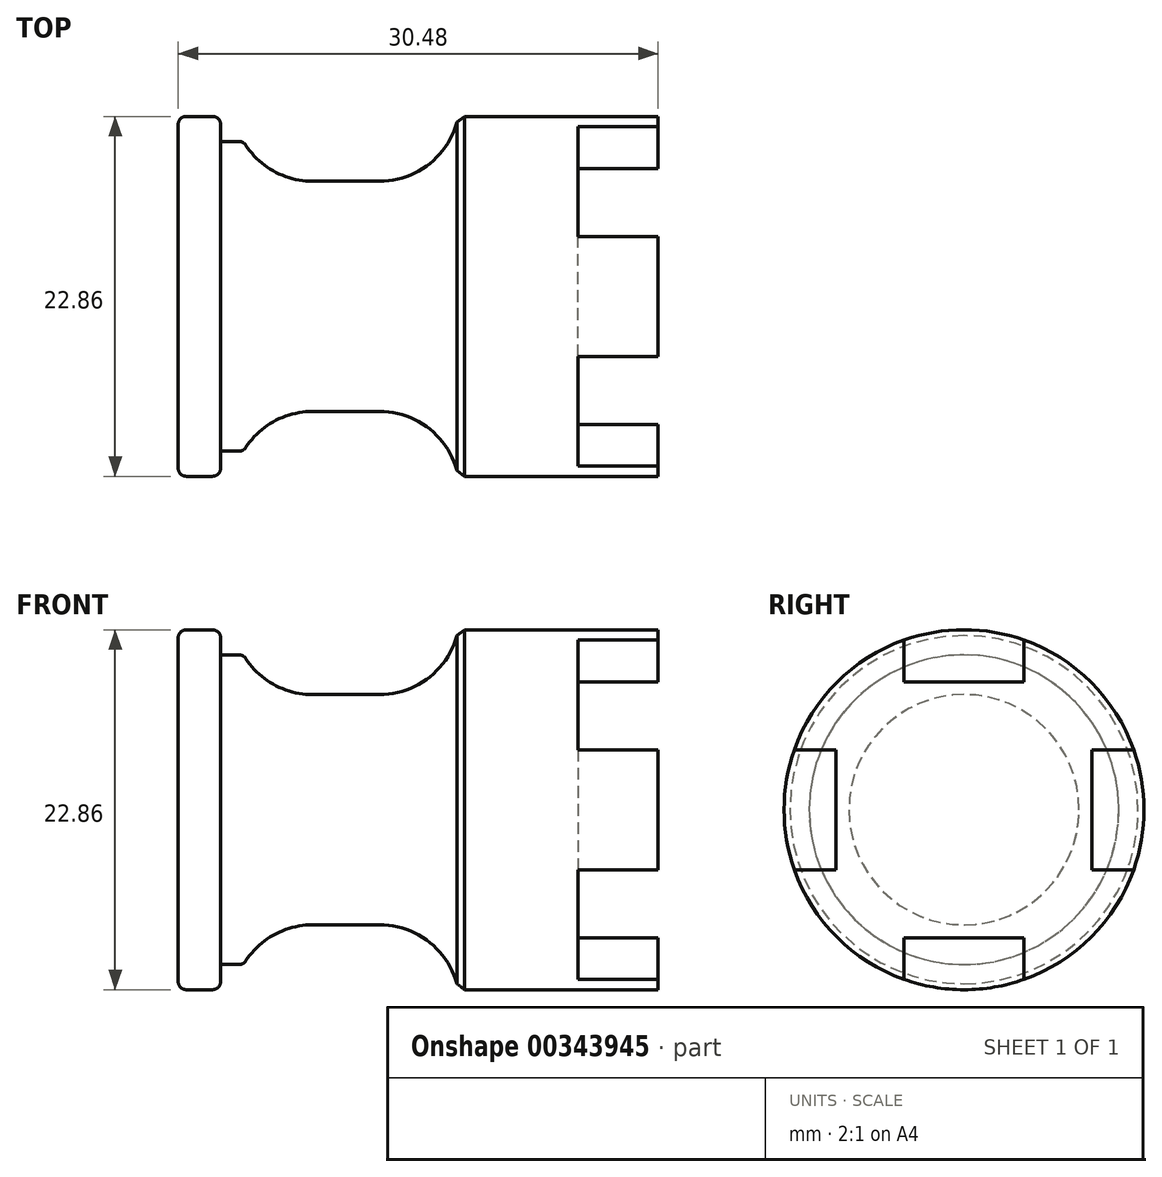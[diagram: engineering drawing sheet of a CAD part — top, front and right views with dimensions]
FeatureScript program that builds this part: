
annotation { "Feature Type Name" : "Feature", "Feature Type Description" : "" }
export const myFeature = defineFeature(function(context is Context, id is Id, definition is map)
    precondition{}
    {
        {
            var Q0;
            Q0=qCreatedBy(makeId("Front.planeOp"),FACE);
            var sketch = newSketch(context, id + "F0", { "sketchPlane" : qUnion([Q0])});
            skLineSegment(sketch, "E0", {"start": v(0, 0) * mm, "end": v(-25.4, 0) * mm});
            skLineSegment(sketch, "E1", {"start": v(-25.4, 0) * mm, "end": v(-25.4, 11.43) * mm});
            skLineSegment(sketch, "E2", {"start": v(-25.4, 11.43) * mm, "end": v(-22.71, 11.43) * mm});
            skLineSegment(sketch, "E3", {"start": v(-22.71, 11.43) * mm, "end": v(-22.71, 9.84) * mm});
            skLineSegment(sketch, "E4", {"start": v(-22.71, 9.84) * mm, "end": v(-21.25, 9.84) * mm});
            skLineSegment(sketch, "E5", {"start": v(-21.25, 9.84) * mm, "end": v(-20.32, 7.31) * mm});
            skLineSegment(sketch, "E6", {"start": v(-20.32, 7.31) * mm, "end": v(-7.62, 7.31) * mm});
            skLineSegment(sketch, "E7", {"start": v(-7.62, 7.31) * mm, "end": v(-7.62, 11.43) * mm});
            skLineSegment(sketch, "E8", {"start": v(-7.62, 11.43) * mm, "end": v(0, 11.43) * mm});
            skLineSegment(sketch, "E9", {"start": v(0, 11.43) * mm, "end": v(0, 0) * mm});
            skSolve(sketch);
        }
        {
            var Q0;
            Q0=makeQuery(id+"F0.imprint","IMPRINT",FACE,{"disambiguationData":[TD([[makeQuery(id+"F0.imprint","IMPRINT",EDGE,{"derivedFrom":sQuery(id+"F0.wireOp",EDGE,"E0")}),-1.0]])]});
            var Q1;
            Q1=sQuery(id+"F0.wireOp",EDGE,"E0");
            revolve(context, id + "F1", {"entities" : qUnion([Q0]), "axis" : qUnion([Q1]), "revolveType" : RevolveType.FULL});
        }
        {
            var Q0;
            Q0=makeQuery(id+"F1.opRevolve","SWEPT_FACE",FACE,{"disambiguationData":[OSD([sQuery(id+"F0.wireOp",EDGE,"E9")])]});
            var sketch = newSketch(context, id + "F2", { "sketchPlane" : qUnion([Q0])});
            skLineSegment(sketch, "E10", {"start": v(-3.81, 10.78) * mm, "end": v(-3.81, 8.13) * mm});
            skLineSegment(sketch, "E11", {"start": v(-3.81, 8.13) * mm, "end": v(3.81, 8.13) * mm});
            skLineSegment(sketch, "E12", {"start": v(3.81, 8.13) * mm, "end": v(3.81, 10.78) * mm});
            skLineSegment(sketch, "E13", {"start": v(10.78, 3.81) * mm, "end": v(8.13, 3.81) * mm});
            skLineSegment(sketch, "E14", {"start": v(8.13, 3.8) * mm, "end": v(8.13, -3.81) * mm});
            skLineSegment(sketch, "E15", {"start": v(8.13, -3.81) * mm, "end": v(10.78, -3.81) * mm});
            skLineSegment(sketch, "E16", {"start": v(-3.81, -10.78) * mm, "end": v(-3.81, -8.13) * mm});
            skLineSegment(sketch, "E17", {"start": v(-3.81, -8.13) * mm, "end": v(3.81, -8.13) * mm});
            skLineSegment(sketch, "E18", {"start": v(3.81, -8.13) * mm, "end": v(3.81, -10.78) * mm});
            skLineSegment(sketch, "E19", {"start": v(-10.78, 3.8) * mm, "end": v(-8.13, 3.8) * mm});
            skLineSegment(sketch, "E20", {"start": v(-8.13, 3.8) * mm, "end": v(-8.13, -3.81) * mm});
            skLineSegment(sketch, "E21", {"start": v(-8.13, -3.81) * mm, "end": v(-10.78, -3.81) * mm});
            skSolve(sketch);
        }
        {
            var Q0;
            {var subQ0=sQuery(id+"F2.wireOp",EDGE,"E10");Q0=makeQuery(id+"F2.imprint","IMPRINT",FACE,{"disambiguationData":[TD([[makeQuery(id+"F2.imprint","IMPRINT",EDGE,{"derivedFrom":subQ0}),1.0]])]});}
            var Q1;
            {var subQ0=sQuery(id+"F2.wireOp",EDGE,"E13");Q1=makeQuery(id+"F2.imprint","IMPRINT",FACE,{"disambiguationData":[TD([[makeQuery(id+"F2.imprint","IMPRINT",EDGE,{"derivedFrom":subQ0}),1.0]])]});}
            var Q2;
            {var subQ0=sQuery(id+"F2.wireOp",EDGE,"E16");Q2=makeQuery(id+"F2.imprint","IMPRINT",FACE,{"disambiguationData":[TD([[makeQuery(id+"F2.imprint","IMPRINT",EDGE,{"derivedFrom":subQ0}),-1.0]])]});}
            var Q3;
            {var subQ0=sQuery(id+"F2.wireOp",EDGE,"E19");Q3=makeQuery(id+"F2.imprint","IMPRINT",FACE,{"disambiguationData":[TD([[makeQuery(id+"F2.imprint","IMPRINT",EDGE,{"derivedFrom":subQ0}),-1.0]])]});}
            extrude(context, id + "F3", {"entities" : qUnion([Q0, Q1, Q2, Q3]), "operationType" : NewBodyOperationType.ADD, "depth" : 5.08 * mm});
        }
        {
            var Q0;
            Q0=makeQuery(id+"F1.opRevolve","SWEPT_EDGE",EDGE,{"disambiguationData":[OSD([sQuery(id+"F0.wireOp",EDGE,"E5"),sQuery(id+"F0.wireOp",EDGE,"E6")])]});
            fillet(context, id + "F4", {"entities" : qUnion([Q0]), "radius" : 5.08 * mm, "tangentPropagation" : true, "allowEdgeOverflow" : false});
        }
        {
            var Q0;
            Q0=makeQuery(id+"F1.opRevolve","SWEPT_EDGE",EDGE,{"disambiguationData":[OSD([sQuery(id+"F0.wireOp",EDGE,"E6"),sQuery(id+"F0.wireOp",EDGE,"E7")])]});
            fillet(context, id + "F5", {"entities" : qUnion([Q0]), "radius" : 5.08 * mm, "tangentPropagation" : true, "allowEdgeOverflow" : false});
        }
        {
            var Q0;
            Q0=makeQuery(id+"F4.opFillet","BLEND_EDGE",EDGE,{"blendedFrom":[makeQuery(id+"F1.opRevolve","SWEPT_EDGE",EDGE,{"disambiguationData":[OSD([sQuery(id+"F0.wireOp",EDGE,"E5"),sQuery(id+"F0.wireOp",EDGE,"E6")])]}),makeQuery(id+"F1.opRevolve","SWEPT_FACE",FACE,{"disambiguationData":[OSD([sQuery(id+"F0.wireOp",EDGE,"E4")])]})],"blendedInto":[makeQuery(id+"F1.opRevolve","SWEPT_FACE",FACE,{"disambiguationData":[OSD([sQuery(id+"F0.wireOp",EDGE,"E4")])]})]});
            var Q1;
            Q1=makeQuery(id+"F1.opRevolve","SWEPT_EDGE",EDGE,{"disambiguationData":[OSD([sQuery(id+"F0.wireOp",EDGE,"E2"),sQuery(id+"F0.wireOp",EDGE,"E3")])]});
            var Q2;
            Q2=makeQuery(id+"F1.opRevolve","SWEPT_EDGE",EDGE,{"disambiguationData":[OSD([sQuery(id+"F0.wireOp",EDGE,"E1"),sQuery(id+"F0.wireOp",EDGE,"E2")])]});
            fillet(context, id + "F6", {"entities" : qUnion([Q0, Q1, Q2]), "radius" : 0.5 * mm, "tangentPropagation" : true, "allowEdgeOverflow" : false});
        }
        {
            var Q0;
            {var subQ0=sQuery(id+"F0.wireOp",EDGE,"E9");var subQ1=sQuery(id+"F0.wireOp",EDGE,"E8");var subQ2=makeQuery(id+"F1.opRevolve","SWEPT_EDGE",EDGE,{"disambiguationData":[OSD([subQ1,subQ0])]});Q0=makeQuery(id+"F5.opFillet","BLEND_EDGE",EDGE,{"blendedFrom":[makeQuery(id+"F1.opRevolve","SWEPT_EDGE",EDGE,{"disambiguationData":[OSD([sQuery(id+"F0.wireOp",EDGE,"E6"),sQuery(id+"F0.wireOp",EDGE,"E7")])]}),makeQuery(id+"F3.boolean.opBoolean","MERGE",FACE,{"derivedFrom":[makeQuery(id+"F1.opRevolve","SWEPT_FACE",FACE,{"disambiguationData":[OSD([subQ1])]}),makeQuery(id+"F3.opExtrude","SWEPT_FACE",FACE,{"disambiguationData":[OSD([subQ1,subQ0]),TDD([makeQuery(id+"F2.imprint","IMPRINT",EDGE,{"disambiguationData":[TD([[makeQuery(id+"F2.imprint","INTERSECT",VERTEX,{"derivedFrom":[subQ2,sQuery(id+"F2.wireOp",EDGE,"E10")]}),1.0]])],"derivedFrom":subQ2})])]}),makeQuery(id+"F3.opExtrude","SWEPT_FACE",FACE,{"disambiguationData":[OSD([subQ1,subQ0]),TDD([makeQuery(id+"F2.imprint","IMPRINT",EDGE,{"disambiguationData":[TD([[makeQuery(id+"F2.imprint","INTERSECT",VERTEX,{"derivedFrom":[subQ2,sQuery(id+"F2.wireOp",EDGE,"E13")]}),1.0]])],"derivedFrom":subQ2})])]}),makeQuery(id+"F3.opExtrude","SWEPT_FACE",FACE,{"disambiguationData":[OSD([subQ1,subQ0]),TDD([makeQuery(id+"F2.imprint","IMPRINT",EDGE,{"disambiguationData":[TD([[makeQuery(id+"F2.imprint","INTERSECT",VERTEX,{"derivedFrom":[subQ2,sQuery(id+"F2.wireOp",EDGE,"E16")]}),-1.0]])],"derivedFrom":subQ2})])]}),makeQuery(id+"F3.opExtrude","SWEPT_FACE",FACE,{"disambiguationData":[OSD([subQ1,subQ0]),TDD([makeQuery(id+"F2.imprint","IMPRINT",EDGE,{"disambiguationData":[TD([[makeQuery(id+"F2.imprint","INTERSECT",VERTEX,{"derivedFrom":[subQ2,sQuery(id+"F2.wireOp",EDGE,"E19")]}),-1.0]])],"derivedFrom":subQ2})])]})]})],"blendedInto":[makeQuery(id+"F3.boolean.opBoolean","MERGE",FACE,{"derivedFrom":[makeQuery(id+"F1.opRevolve","SWEPT_FACE",FACE,{"disambiguationData":[OSD([subQ1])]}),makeQuery(id+"F3.opExtrude","SWEPT_FACE",FACE,{"disambiguationData":[OSD([subQ1,subQ0]),TDD([makeQuery(id+"F2.imprint","IMPRINT",EDGE,{"disambiguationData":[TD([[makeQuery(id+"F2.imprint","INTERSECT",VERTEX,{"derivedFrom":[subQ2,sQuery(id+"F2.wireOp",EDGE,"E10")]}),1.0]])],"derivedFrom":subQ2})])]}),makeQuery(id+"F3.opExtrude","SWEPT_FACE",FACE,{"disambiguationData":[OSD([subQ1,subQ0]),TDD([makeQuery(id+"F2.imprint","IMPRINT",EDGE,{"disambiguationData":[TD([[makeQuery(id+"F2.imprint","INTERSECT",VERTEX,{"derivedFrom":[subQ2,sQuery(id+"F2.wireOp",EDGE,"E13")]}),1.0]])],"derivedFrom":subQ2})])]}),makeQuery(id+"F3.opExtrude","SWEPT_FACE",FACE,{"disambiguationData":[OSD([subQ1,subQ0]),TDD([makeQuery(id+"F2.imprint","IMPRINT",EDGE,{"disambiguationData":[TD([[makeQuery(id+"F2.imprint","INTERSECT",VERTEX,{"derivedFrom":[subQ2,sQuery(id+"F2.wireOp",EDGE,"E16")]}),-1.0]])],"derivedFrom":subQ2})])]}),makeQuery(id+"F3.opExtrude","SWEPT_FACE",FACE,{"disambiguationData":[OSD([subQ1,subQ0]),TDD([makeQuery(id+"F2.imprint","IMPRINT",EDGE,{"disambiguationData":[TD([[makeQuery(id+"F2.imprint","INTERSECT",VERTEX,{"derivedFrom":[subQ2,sQuery(id+"F2.wireOp",EDGE,"E19")]}),-1.0]])],"derivedFrom":subQ2})])]})]})]});}
            chamfer(context, id + "F7", {"entities" : qUnion([Q0]), "width" : 0.5 * mm, "tangentPropagation" : true});
        }
    });
